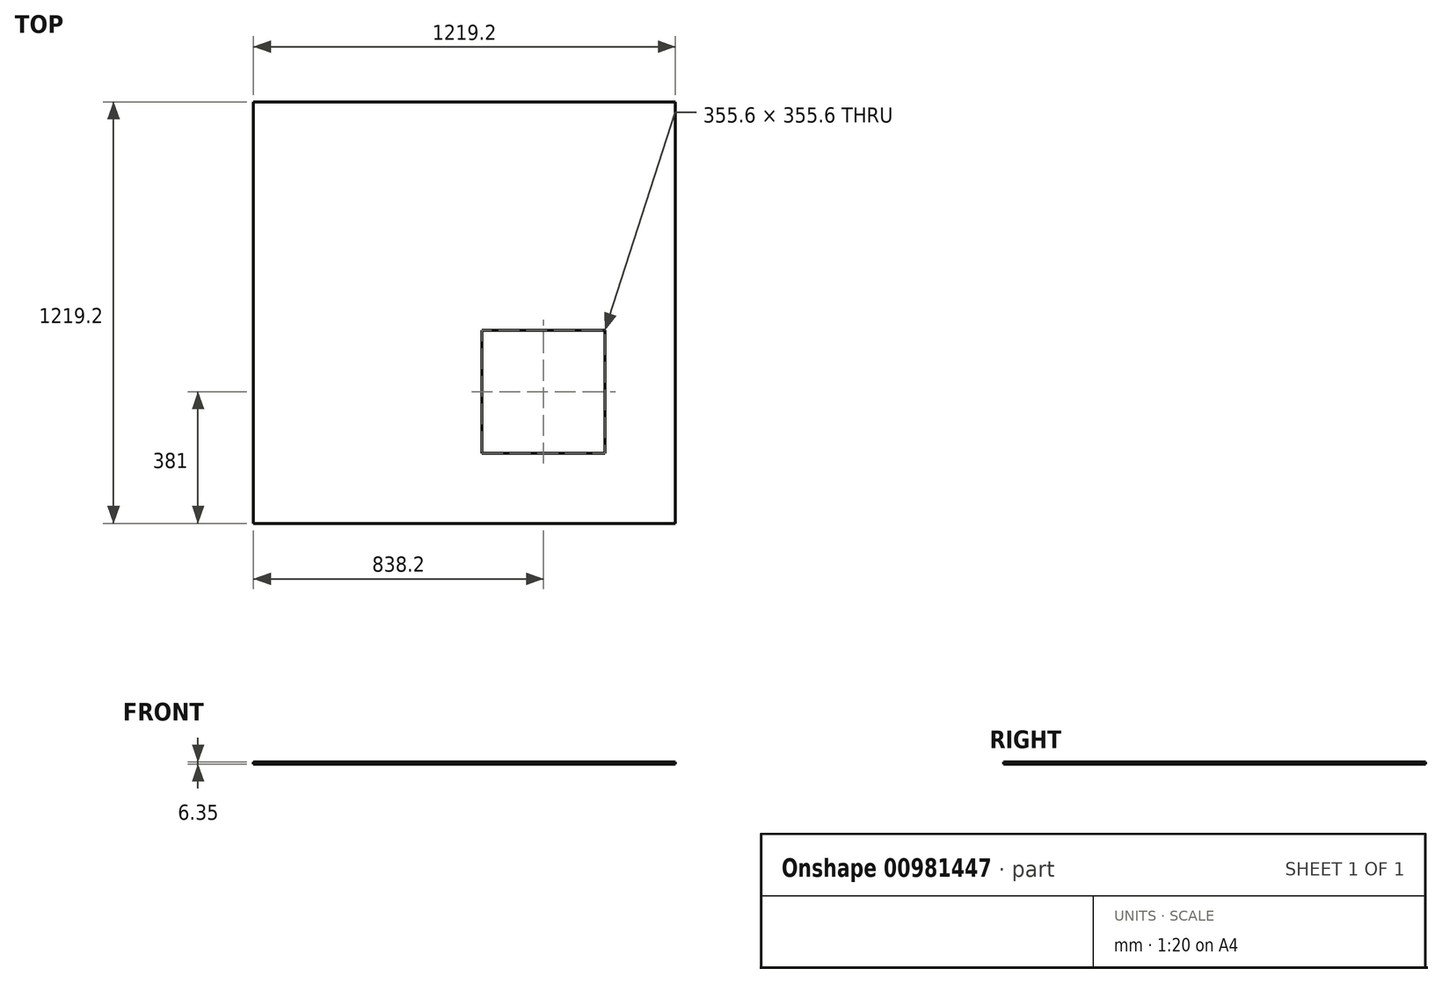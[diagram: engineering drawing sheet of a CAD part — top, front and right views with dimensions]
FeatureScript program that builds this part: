
annotation { "Feature Type Name" : "Feature", "Feature Type Description" : "" }
export const myFeature = defineFeature(function(context is Context, id is Id, definition is map)
    precondition{}
    {
        {
            var Q0;
            Q0=qCreatedBy(makeId("Top.planeOp"),FACE);
            var sketch = newSketch(context, id + "F0", { "sketchPlane" : qUnion([Q0])});
            skLineSegment(sketch, "E0.bottom", {"start": v(-609.6, 609.6) * mm, "end": v(609.6, 609.6) * mm});
            skLineSegment(sketch, "E0.top", {"start": v(-609.6, -609.6) * mm, "end": v(609.6, -609.6) * mm});
            skLineSegment(sketch, "E0.left", {"start": v(-609.6, 609.6) * mm, "end": v(-609.6, -609.6) * mm});
            skLineSegment(sketch, "E0.right", {"start": v(609.6, 609.6) * mm, "end": v(609.6, -609.6) * mm});
            skLineSegment(sketch, "E1", {"start": v(-609.6, 609.6) * mm, "end": v(609.6, -609.6) * mm});
            skLineSegment(sketch, "E2", {"start": v(0, 0) * mm, "end": v(0, 0) * mm});
            skSolve(sketch);
        }
        {
            var Q0;
            Q0=qSketchRegion(id+"F0",true);
            extrude(context, id + "F1", {"entities" : qUnion([Q0]), "depth" : 6.35 * mm, "offsetDistance" : 25.4 * mm});
        }
        {
            var Q0;
            Q0=qCreatedBy(makeId("Top.planeOp"),FACE);
            var sketch = newSketch(context, id + "F2", { "sketchPlane" : qUnion([Q0])});
            skLineSegment(sketch, "E3.bottom", {"start": v(50.8, -50.8) * mm, "end": v(406.4, -50.8) * mm});
            skLineSegment(sketch, "E3.top", {"start": v(50.8, -406.4) * mm, "end": v(406.4, -406.4) * mm});
            skLineSegment(sketch, "E3.left", {"start": v(50.8, -50.8) * mm, "end": v(50.8, -406.4) * mm});
            skLineSegment(sketch, "E3.right", {"start": v(406.4, -50.8) * mm, "end": v(406.4, -406.4) * mm});
            skSolve(sketch);
        }
        {
            var Q0;
            Q0 = qSketchRegion(id + "F2", true);
            extrude(context, id + "F3", {"entities" : qUnion([Q0]), "operationType" : NewBodyOperationType.REMOVE, "depth" : 25.4 * mm, "offsetDistance" : 25.4 * mm});
        }
    });
